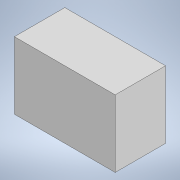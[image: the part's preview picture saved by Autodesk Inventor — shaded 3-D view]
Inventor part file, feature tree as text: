
AUTODESK INVENTOR PART (.ipt)
format: ipt  version: 2022 (Build 260153000, 153)  size: 87,040 bytes
history: native  units: mm
features: other x1, extrude x1, sketch x1
ambient origin geometry x8: Origin, YZ Plane, XZ Plane, XY Plane, X Axis, Y Axis, Z Axis, Center Point
bodies: Body1 (feature_tree)
feature tree (3):
  other  "ソリッド1"
  extrude  "押し出し1"  Depth=3000.0mm
  sketch  "スケッチ1"
